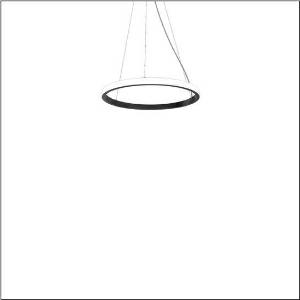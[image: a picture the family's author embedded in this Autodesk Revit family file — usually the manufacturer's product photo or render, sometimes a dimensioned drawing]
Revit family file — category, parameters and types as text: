
# Revit family: silica_r__21_ring-o_5pjbo1d3104a_0aff
name_source: partatom
category: Lighting Fixtures
units: mm (PartAtom-declared; Revit-internal decimal feet)

## family parameters
Cut with Voids When Loaded = No
Host = Face
Light Source = No
Part Type = Normal
Room Calculation Point = No
Round Connector Dimension = Use Diameter
Shared = No

## types (1)
- Silica® 21 Ring-O (1 x LED, 3930 lm, 60 W, 4000K)
    Apparent Load = 60 VA
    CIE Flux Codes = 2 16 49 50 100
    Color Rendering = 80
    Color Temperature = 4000K
    Default Elevation = 1800 mm
    Description = Silica® 21 Ring-O, suspended luminaire, of PMMA, frosted, light emission: outer ring side luminous distribution, primary light characteristic: symmetric, installation type: suspended mounting, LED, rated luminous flux: 3.930lm, luminous efficacy: 66lm/W, light colour: 840, colour temperature: 4000K, control gear: DALI 2, with terminal, 5-pole, mains connection: 230V, AC/DC, 0/50..60Hz, rated input power: 60W, housing, of extruded aluminium section, jet black (RAL 9005), diameter: 610mm, ceiling canopy, jet black (RAL 9005), protection rating (lamp compartment): IP40, insulation class (complete): insulation class I (protective earthing), certification: CE, impact resistance: IK02, permissible operating ambient temperature: 0..+35°C, packaging unit: 1 piece
    Height = 48 mm  [stored 0.15748 ft]
    Lamp = 1 x LED
    Lamp Light Flux = 3930 lm
    Lamp Power = 60 W
    Lamp count = 1
    Length = 610 mm
    Luminous efficacy = 66 lm/W
    Manufacturer = Siteco
    ModVariant = No
    Model = 5PJBO1D3104A
    Mounting Place = Ceiling
    Mounting Type = Pendant
    Number of Poles = 1
    OnlyDefault = Yes
    Power Factor = 1
    Product Name = Silica® 21 Ring-O
    Product group = suspended luminaire
    ProductGroupID = 905
    Protection Class = Protection class I
    Protection Degree = IP 40
    RLX_Detail_Level = 1
    RLX_Emergency_Light_Flux = 0 lm
    RLX_Emergency_Type = 0
    RLX_Emergency_Type_DB = No
    RlxData = <blob elided: 12173 chars, md5=09530843>
    Socket = socket
    Standby Power = 0 W
    System Light Flux = 3930 lm
    System Power = 60 W
    Type Comments = Product without accessories
    Type Image = l_1258377.jpg
    URL = http://relux.com
    VarID = ---
    Voltage = 0 V
    Weight = 0.00 kg
    Width = 0 mm  [stored 0 ft]

note: [stored X ft] marks values corroborated as IEEE doubles in the binary element streams (Revit-internal decimal feet)

## geometry (parser evidence)
native form markers: Sweep x10
no freeform markers — native parametric forms only
